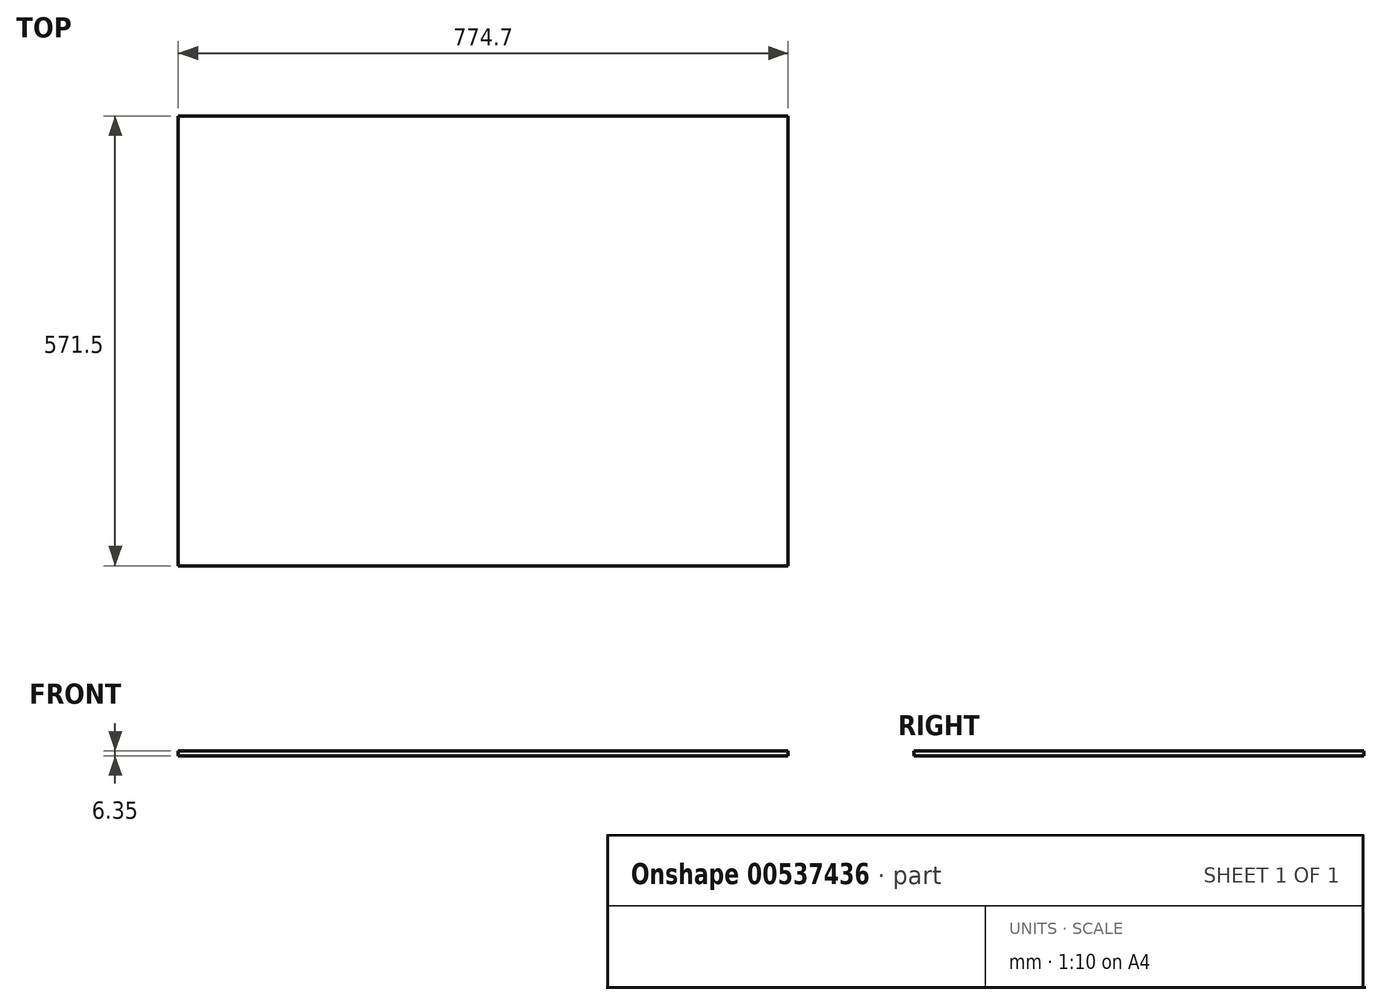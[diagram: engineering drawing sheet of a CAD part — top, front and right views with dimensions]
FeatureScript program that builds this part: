
annotation { "Feature Type Name" : "Feature", "Feature Type Description" : "" }
export const myFeature = defineFeature(function(context is Context, id is Id, definition is map)
    precondition{}
    {
        {
            var Q0;
            Q0=qCreatedBy(makeId("Top.planeOp"),FACE);
            var sketch = newSketch(context, id + "F0", { "sketchPlane" : qUnion([Q0])});
            skLineSegment(sketch, "E0.bottom", {"start": v(387.35, 285.75) * mm, "end": v(-387.35, 285.75) * mm});
            skLineSegment(sketch, "E0.top", {"start": v(387.35, -285.75) * mm, "end": v(-387.35, -285.75) * mm});
            skLineSegment(sketch, "E0.left", {"start": v(387.35, 285.75) * mm, "end": v(387.35, -285.75) * mm});
            skLineSegment(sketch, "E0.right", {"start": v(-387.35, 285.75) * mm, "end": v(-387.35, -285.75) * mm});
            skPoint(sketch, "E0.middle", {"position": v(0, 0) * mm});
            skSolve(sketch);
        }
        {
            var Q0;
            Q0 = qSketchRegion(id + "F0", true);
            extrude(context, id + "F1", {"entities" : qUnion([Q0]), "depth" : 6.35 * mm, "offsetDistance" : 25.4 * mm});
        }
    });
